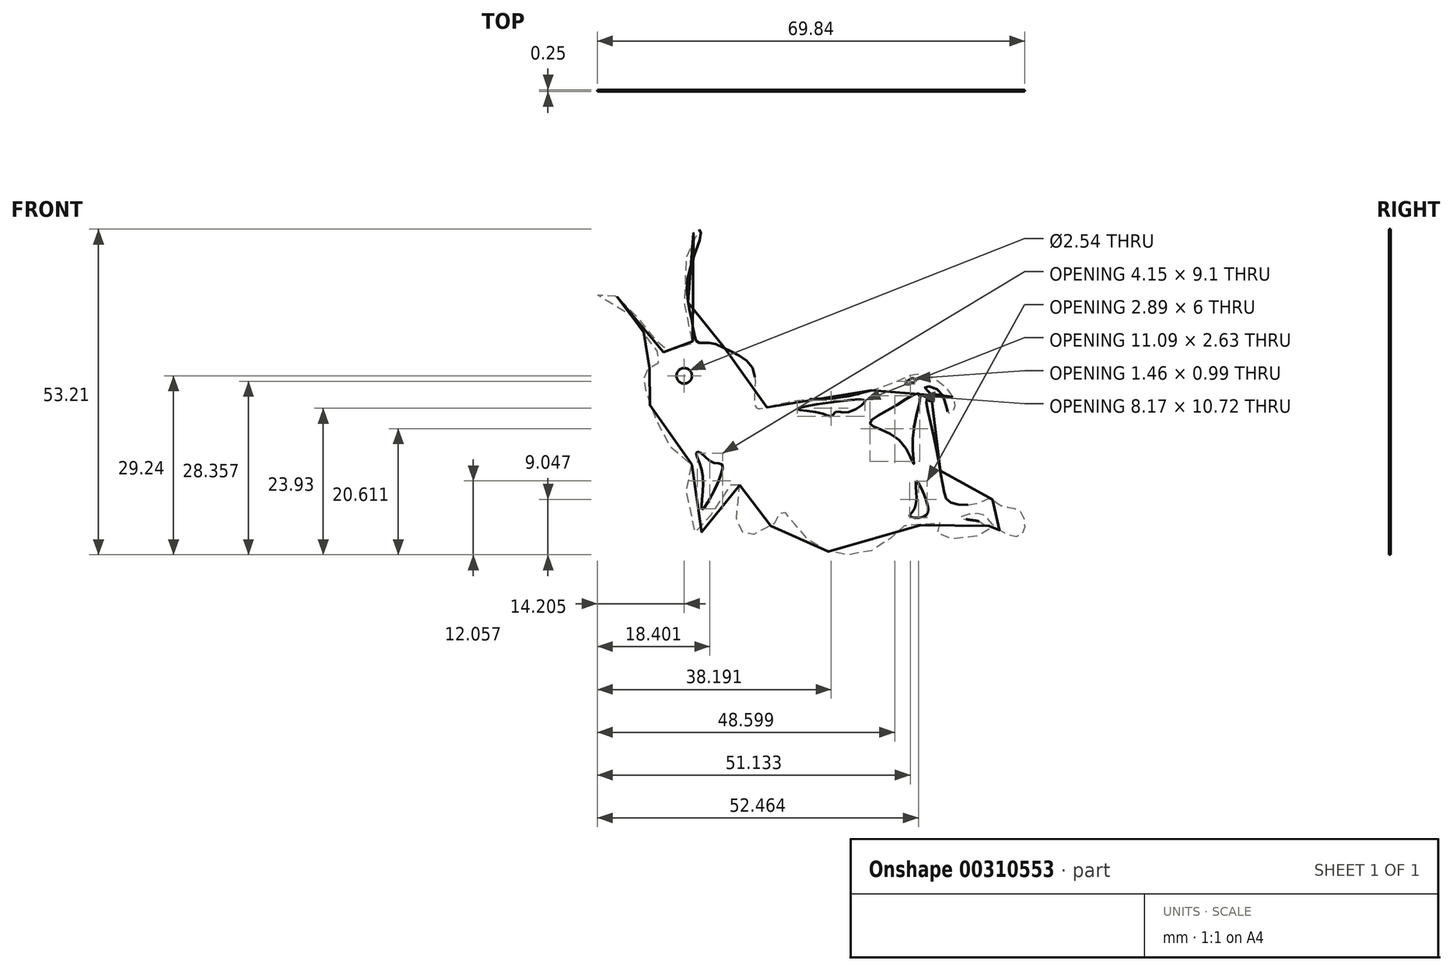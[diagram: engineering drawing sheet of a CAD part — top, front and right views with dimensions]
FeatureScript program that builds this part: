
annotation { "Feature Type Name" : "Feature", "Feature Type Description" : "" }
export const myFeature = defineFeature(function(context is Context, id is Id, definition is map)
    precondition{}
    {
        {
            var Q0;
            Q0=qCreatedBy(makeId("Front.planeOp"),FACE);
            var sketch = newSketch(context, id + "F0", { "sketchPlane" : qUnion([Q0])});
            skFitSpline(sketch, "E0", {"points": [v(-16.77, -1.7) * mm, v(-17.68, 0) * mm, v(-18.6, -2.75) * mm, v(-21.6, -6.8) * mm, v(-23.55, -9.92) * mm, v(-24.99, -5.62) * mm, v(-25.38, 0) * mm, v(-24.6, 1.55) * mm, v(-24.73, 2.07) * mm, v(-28.38, 4.81) * mm, v(-29.94, 7.81) * mm, v(-31.38, 11.2) * mm, v(-31.9, 14.46) * mm, v(-31.5, 14.99) * mm, v(-32.42, 15.77) * mm, v(-31.25, 16.29) * mm, v(-32.16, 17.07) * mm, v(-31.12, 17.6) * mm, v(-31.12, 18.25) * mm, v(-29.94, 18.25) * mm, v(-30.73, 18.77) * mm, v(-29.94, 19.16) * mm, v(-30.99, 21.25) * mm, v(-36.72, 27.9) * mm, v(-40.03, 29.46) * mm, v(-38.55, 29.85) * mm, v(-36.72, 28.94) * mm, v(-34.5, 26.85) * mm, v(-32.16, 24.11) * mm, v(-29.81, 20.98) * mm, v(-29.03, 19.94) * mm, v(-28.38, 20.33) * mm, v(-27.99, 21.11) * mm, v(-26.03, 20.85) * mm, v(-26.03, 21.5) * mm, v(-25.12, 21.77) * mm, v(-24.47, 21.38) * mm, v(-25.38, 25.68) * mm, v(-25.64, 34.16) * mm, v(-23.94, 39.93) * mm, v(-23.16, 39.93) * mm, v(-24.07, 36.11) * mm, v(-25.38, 30.5) * mm, v(-24.47, 24.5) * mm, v(-23.81, 21.77) * mm, v(-23.16, 21.5) * mm, v(-21.47, 21.5) * mm, v(-17.81, 19.94) * mm, v(-14.42, 16.81) * mm, v(-14.16, 11.07) * mm, v(-12.08, 11.07) * mm, v(-6.34, 12.25) * mm, v(0, 12.64) * mm, v(9.18, 15.38) * mm, v(12.31, 16.42) * mm, v(16.35, 14.72) * mm, v(18.3, 10.94) * mm, v(17.4, 10.03) * mm, v(15.96, 13.55) * mm, v(13.48, 14.2) * mm, v(15.05, 12.5) * mm, v(14.4, 11.99) * mm, v(13.75, 12.25) * mm, v(14.79, 6.77) * mm, v(16.48, -2.23) * mm, v(17.66, -4.58) * mm, v(22.35, -4.58) * mm, v(24.18, -3.92) * mm, v(26, -5.1) * mm, v(29.15, -6.14) * mm, v(29.15, -9.92) * mm, v(24.57, -8.23) * mm, v(22.48, -6.4) * mm, v(19.22, -7.05) * mm, v(23, -7.84) * mm, v(23.92, -9.27) * mm, v(15.7, -9.92) * mm, v(15.96, -7.97) * mm, v(11.79, -8.36) * mm, v(10.62, -8.1) * mm, v(5.66, -12) * mm, v(-3.86, -11.88) * mm, v(-8.69, -6.92) * mm, v(-9.99, -6.01) * mm, v(-10.9, -7.84) * mm, v(-12.6, -8.75) * mm, v(-15.34, -9.92) * mm, v(-17.3, -7.18) * mm, v(-16.77, -1.7) * mm]});
            skFitSpline(sketch, "E1", {"points": [v(4.49, 8.33) * mm, v(8.4, 11.07) * mm, v(12.57, 13.16) * mm, v(11.53, 6.5) * mm, v(11.66, 1.68) * mm, v(9.18, 5.73) * mm, v(4.49, 8.33) * mm]});
            skFitSpline(sketch, "E2", {"points": [v(-23.03, 3.5) * mm, v(-21.07, 1.94) * mm, v(-19.64, 1.68) * mm, v(-21.34, -3.4) * mm, v(-22.9, -5.62) * mm, v(-22.77, -2.36) * mm, v(-23.3, 1.81) * mm, v(-23.81, 3.64) * mm, v(-23.03, 3.5) * mm]});
            skFitSpline(sketch, "E3", {"points": [v(12.05, -1.06) * mm, v(11.92, -5.23) * mm, v(11, -6.8) * mm, v(13.48, -6.8) * mm, v(13.75, -4.32) * mm, v(12.05, -1.06) * mm]});
            skFitSpline(sketch, "E4", {"points": [v(-7.39, 10.71) * mm, v(-3.43, 10.01) * mm, v(-1.8, 9.55) * mm, v(-1.03, 10.25) * mm, v(0.68, 10.17) * mm, v(3.7, 11.95) * mm, v(0, 12.03) * mm, v(-7.39, 10.71) * mm]});
            skFitSpline(sketch, "E5", {"points": [v(10.37, 14.82) * mm, v(11.46, 15.75) * mm, v(11.84, 15.29) * mm, v(10.37, 14.82) * mm]});
            skCircle(sketch, "E6", {"center": v(-25.82, 16.14) * mm, "radius": 1.27 * mm});
            skSolve(sketch);
        }
        {
            var Q0;
            Q0 = qSketchRegion(id + "F0", true);
            extrude(context, id + "F1", {"entities" : qUnion([Q0]), "depth" : 0.25 * mm});
        }
    });
